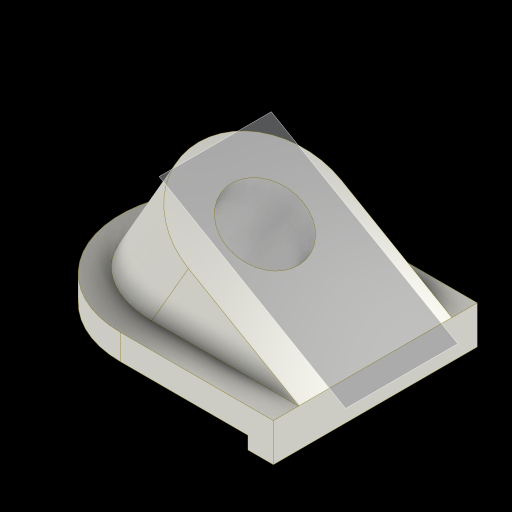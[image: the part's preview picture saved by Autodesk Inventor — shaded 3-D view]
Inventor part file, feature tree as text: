
AUTODESK INVENTOR PART (.ipt)
format: ipt  version: 2024 (Build 280153000, 153)  size: 172,544 bytes
history: native  units: in
note: dims shown in document units (in); Inventor stores cm internally (conversion verified against a paired STEP export)
features: extrude x4, sketch x3, other x1
ambient origin geometry x8: Origin, YZ Plane, XZ Plane, XY Plane, X Axis, Y Axis, Z Axis, Center Point
bodies: Solid1 (feature_tree)
feature tree (8):
  extrude  "BASE"  Depth=3.0in
  extrude  "LIP"  Depth=0.25in
  other  "ANGLE PLANE"
  sketch  "Sketch3"  dims[d5=0.5in d6=0.0in d7=30.0deg d8=3.0in d10=1.5in d11=2.5in d12=0.5in d13=0.0in d14=0.0in d15=0.0in d16=0.0in]
  extrude  "AGNLED FACE"  TaperAngle=30.0deg  [1 undecoded]
  extrude  "HOLE"  Depth=3.0in
  sketch  "Sketch1"  dims[d0=4.0in d1=3.0in]
  sketch  "Sketch2"  dims[d2=0.5in d3=0.0in d4=0.25in]
note: 1 required parameter value undecoded (feature->parameter linkage not recoverable at this tier; creation-order binding heuristic only, values carry confidence <= 0.55)
